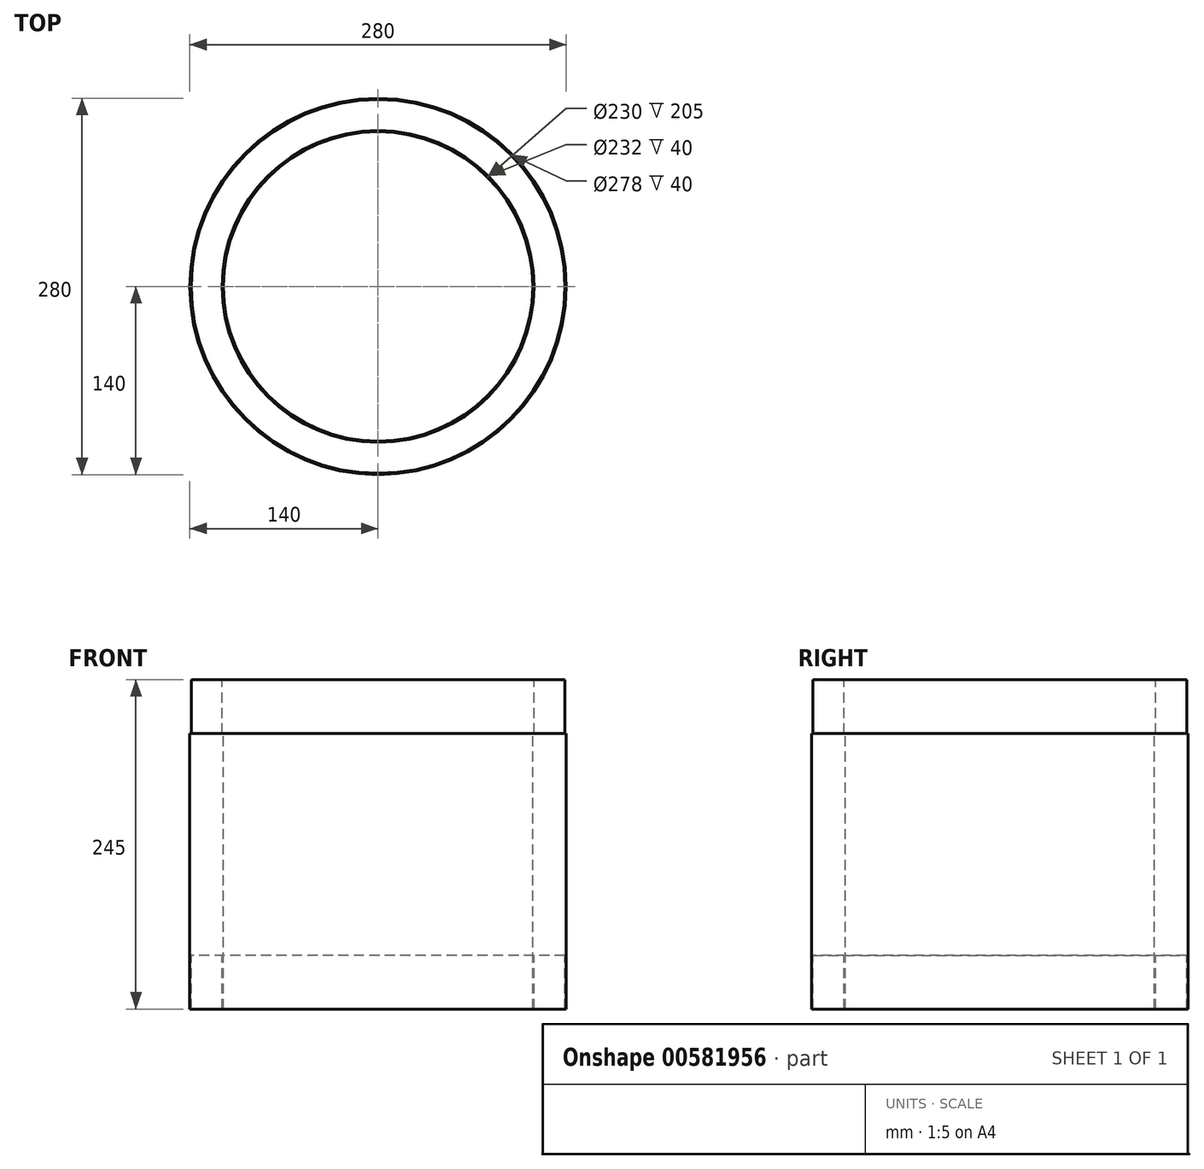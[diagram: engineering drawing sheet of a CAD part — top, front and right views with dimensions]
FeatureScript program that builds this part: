
annotation { "Feature Type Name" : "Feature", "Feature Type Description" : "" }
export const myFeature = defineFeature(function(context is Context, id is Id, definition is map)
    precondition{}
    {
        {
            var Q0;
            Q0=qCreatedBy(makeId("Front.planeOp"),FACE);
            var sketch = newSketch(context, id + "F0", { "sketchPlane" : qUnion([Q0])});
            skLineSegment(sketch, "E0", {"start": v(0, 345.75) * mm, "end": v(0, -558.03) * mm, "construction": true});
            skLineSegment(sketch, "E1", {"start": v(-115, -518.84) * mm, "end": v(-115, -313.84) * mm});
            skLineSegment(sketch, "E2", {"start": v(-115, -313.84) * mm, "end": v(-116, -313.84) * mm});
            skLineSegment(sketch, "E3", {"start": v(-116, -313.84) * mm, "end": v(-116, -273.84) * mm});
            skLineSegment(sketch, "E4", {"start": v(-116, -273.84) * mm, "end": v(-139, -273.84) * mm});
            skLineSegment(sketch, "E5", {"start": v(-139, -273.84) * mm, "end": v(-139, -313.84) * mm});
            skLineSegment(sketch, "E6", {"start": v(-139, -313.84) * mm, "end": v(-140, -313.84) * mm});
            skLineSegment(sketch, "E7", {"start": v(-140, -313.84) * mm, "end": v(-140, -518.84) * mm});
            skLineSegment(sketch, "E8", {"start": v(-140, -518.84) * mm, "end": v(-139, -518.84) * mm});
            skLineSegment(sketch, "E9", {"start": v(-139, -518.84) * mm, "end": v(-139, -478.84) * mm});
            skLineSegment(sketch, "E10", {"start": v(-139, -478.84) * mm, "end": v(-116, -478.84) * mm});
            skLineSegment(sketch, "E11", {"start": v(-116, -478.84) * mm, "end": v(-116, -518.84) * mm});
            skLineSegment(sketch, "E12", {"start": v(-116, -518.84) * mm, "end": v(-115, -518.84) * mm});
            skSolve(sketch);
        }
        {
            var Q0;
            Q0=qSketchRegion(id+"F0",true);
            var Q1;
            Q1=sQuery(id+"F0.wireOp",EDGE,"E0");
            revolve(context, id + "F1", {"entities" : qUnion([Q0]), "axis" : qUnion([Q1]), "revolveType" : RevolveType.FULL});
        }
    });
